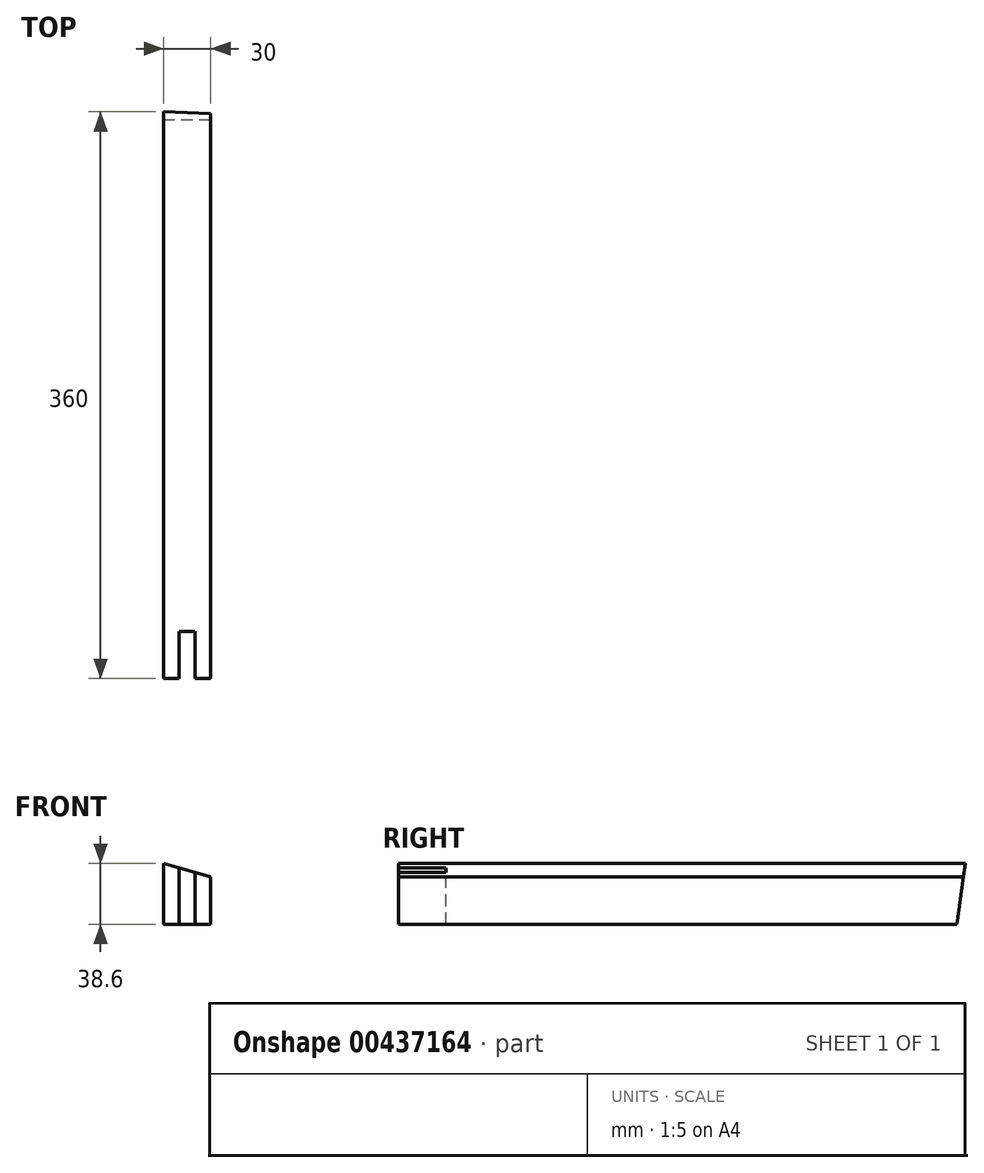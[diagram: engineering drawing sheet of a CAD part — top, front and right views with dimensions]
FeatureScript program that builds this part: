
annotation { "Feature Type Name" : "Feature", "Feature Type Description" : "" }
export const myFeature = defineFeature(function(context is Context, id is Id, definition is map)
    precondition{}
    {
        {
            var Q0;
            Q0=qCreatedBy(makeId("Front.planeOp"),FACE);
            var sketch = newSketch(context, id + "F0", { "sketchPlane" : qUnion([Q0])});
            skLineSegment(sketch, "E0", {"start": v(0, 0) * mm, "end": v(0, 30) * mm});
            skLineSegment(sketch, "E1", {"start": v(0, 0) * mm, "end": v(-30, 0) * mm});
            skLineSegment(sketch, "E2", {"start": v(-30, 0) * mm, "end": v(-30, 38.6) * mm});
            skLineSegment(sketch, "E3", {"start": v(0, 30) * mm, "end": v(-30, 38.6) * mm});
            skPoint(sketch, "E4.orphan", {"position": v(-30, 30) * mm});
            skSolve(sketch);
        }
        {
            var Q0;
            Q0 = qSketchRegion(id + "F0", true);
            extrude(context, id + "F1", {"entities" : qUnion([Q0]), "depth" : 360 * mm});
        }
        {
            var Q0;
            Q0=makeQuery(id+"F1.opExtrude","SWEPT_FACE",FACE,{"disambiguationData":[OSD([sQuery(id+"F0.wireOp",EDGE,"E2")])]});
            var sketch = newSketch(context, id + "F2", { "sketchPlane" : qUnion([Q0])});
            skLineSegment(sketch, "E5", {"start": v(0, 38.6) * mm, "end": v(5.43, 0) * mm});
            skLineSegment(sketch, "E6", {"start": v(0, 38.6) * mm, "end": v(0, 0) * mm});
            skLineSegment(sketch, "E7", {"start": v(0, 0) * mm, "end": v(5.43, 0) * mm});
            skSolve(sketch);
        }
        {
            var Q0;
            Q0 = qSketchRegion(id + "F2", true);
            extrude(context, id + "F3", {"entities" : qUnion([Q0]), "operationType" : NewBodyOperationType.REMOVE, "oppositeDirection" : true, "depth" : 30 * mm});
        }
        {
            var Q0;
            Q0=makeQuery(id+"F1.opExtrude","CAP_FACE",FACE,{"disambiguationData":[OSD([sQuery(id+"F0.wireOp",EDGE,"E0"),sQuery(id+"F0.wireOp",EDGE,"E1"),sQuery(id+"F0.wireOp",EDGE,"E2"),sQuery(id+"F0.wireOp",EDGE,"E3")])],"isStart":false});
            var sketch = newSketch(context, id + "F4", { "sketchPlane" : qUnion([Q0])});
            skLineSegment(sketch, "E8", {"start": v(-15, 0) * mm, "end": v(-10, 0) * mm});
            skPoint(sketch, "E8.endSnap0", {"position": v(-15, 0) * mm});
            skLineSegment(sketch, "E9", {"start": v(-10, 0) * mm, "end": v(-10, 32.87) * mm});
            skLineSegment(sketch, "E10", {"start": v(-15, 34.3) * mm, "end": v(-10, 32.87) * mm});
            skLineSegment(sketch, "E11", {"start": v(-15, 0) * mm, "end": v(-20, 0) * mm});
            skLineSegment(sketch, "E12", {"start": v(-20, 0) * mm, "end": v(-20, 35.73) * mm});
            skLineSegment(sketch, "E13", {"start": v(-20, 35.73) * mm, "end": v(-15, 34.3) * mm});
            skSolve(sketch);
        }
        {
            var Q0;
            Q0 = qSketchRegion(id + "F4", true);
            extrude(context, id + "F5", {"entities" : qUnion([Q0]), "operationType" : NewBodyOperationType.REMOVE, "oppositeDirection" : true, "depth" : 30 * mm});
        }
    });
